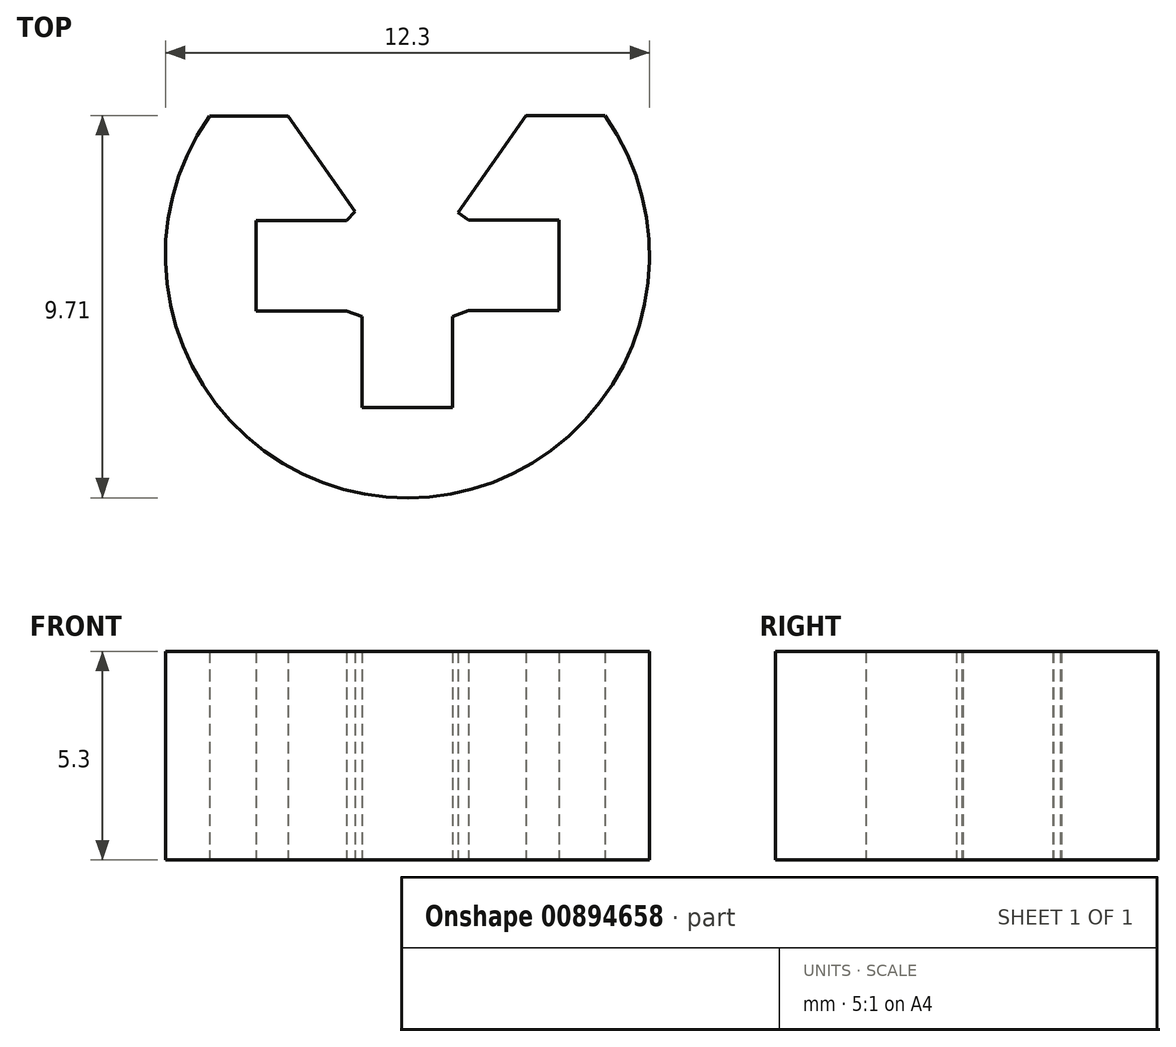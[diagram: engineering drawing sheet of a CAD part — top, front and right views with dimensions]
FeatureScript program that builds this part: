
annotation { "Feature Type Name" : "Feature", "Feature Type Description" : "" }
export const myFeature = defineFeature(function(context is Context, id is Id, definition is map)
    precondition{}
    {
        {
            var Q0;
            Q0=qCreatedBy(makeId("Top.planeOp"),FACE);
            var sketch = newSketch(context, id + "F0", { "sketchPlane" : qUnion([Q0])});
            skCircle(sketch, "E0", {"center": v(0, 0) * mm, "radius": 6.15 * mm});
            skLineSegment(sketch, "E1", {"start": v(-0.01, -0.76) * mm, "end": v(-6.07, 7.88) * mm});
            skLineSegment(sketch, "E2", {"start": v(-6.07, 7.88) * mm, "end": v(6.04, 7.88) * mm});
            skLineSegment(sketch, "E3", {"start": v(6.04, 7.88) * mm, "end": v(-0.01, -0.76) * mm});
            skPoint(sketch, "E4", {"position": v(-0.01, 7.88) * mm});
            skLineSegment(sketch, "E5", {"start": v(-5.03, 3.54) * mm, "end": v(-3.03, 3.54) * mm});
            skLineSegment(sketch, "E6", {"start": v(3.01, 3.56) * mm, "end": v(5.01, 3.56) * mm});
            skArc(sketch, "E7", {"start": v(-3.88, 4.77) * mm, "mid": v(-4.51, 4.21) * mm, "end": v(-5.03, 3.54) * mm});
            skArc(sketch, "E8", {"start": v(5.01, 3.56) * mm, "mid": v(4.46, 4.18) * mm, "end": v(3.87, 4.78) * mm});
            skLineSegment(sketch, "E9.bottom", {"start": v(3.85, 0.91) * mm, "end": v(1.55, 0.91) * mm});
            skLineSegment(sketch, "E9.top", {"start": v(3.85, -1.39) * mm, "end": v(1.55, -1.39) * mm});
            skLineSegment(sketch, "E9.left", {"start": v(3.85, 0.91) * mm, "end": v(3.85, -1.39) * mm});
            skLineSegment(sketch, "E9.right", {"start": v(1.55, 0.91) * mm, "end": v(1.55, -1.39) * mm});
            skPoint(sketch, "E9.middle", {"position": v(2.7, -0.24) * mm});
            skLineSegment(sketch, "E10.bottom", {"start": v(1.15, -3.85) * mm, "end": v(-1.15, -3.85) * mm});
            skLineSegment(sketch, "E10.top", {"start": v(1.15, -1.55) * mm, "end": v(-1.15, -1.55) * mm});
            skLineSegment(sketch, "E10.left", {"start": v(1.15, -3.85) * mm, "end": v(1.15, -1.55) * mm});
            skLineSegment(sketch, "E10.right", {"start": v(-1.15, -3.85) * mm, "end": v(-1.15, -1.55) * mm});
            skPoint(sketch, "E10.middle", {"position": v(0, -2.7) * mm});
            skLineSegment(sketch, "E11.bottom", {"start": v(-1.55, -1.4) * mm, "end": v(-3.85, -1.4) * mm});
            skLineSegment(sketch, "E11.top", {"start": v(-1.55, 0.9) * mm, "end": v(-3.85, 0.9) * mm});
            skLineSegment(sketch, "E11.left", {"start": v(-1.55, -1.4) * mm, "end": v(-1.55, 0.9) * mm});
            skLineSegment(sketch, "E11.right", {"start": v(-3.85, -1.4) * mm, "end": v(-3.85, 0.9) * mm});
            skPoint(sketch, "E11.middle", {"position": v(-2.7, -0.26) * mm});
            skLineSegment(sketch, "E12", {"start": v(-1.55, -1.4) * mm, "end": v(-1.15, -1.55) * mm});
            skLineSegment(sketch, "E13", {"start": v(-1.55, 0.9) * mm, "end": v(-1.27, 1.18) * mm});
            skLineSegment(sketch, "E14", {"start": v(1.55, -1.39) * mm, "end": v(1.15, -1.55) * mm});
            skLineSegment(sketch, "E15", {"start": v(1.55, 0.91) * mm, "end": v(1.16, 1.18) * mm});
            skSolve(sketch);
        }
        {
            var Q0;
            {var subQ2=sQuery(id+"F0.wireOp",EDGE,"E5");Q0=makeQuery(id+"F0.imprint","IMPRINT",FACE,{"disambiguationData":[TD([[makeQuery(id+"F0.imprint","IMPRINT",EDGE,{"derivedFrom":subQ2}),-1.0]])]});}
            extrude(context, id + "F1", {"entities" : qUnion([Q0]), "depth" : 5.3 * mm, "offsetDistance" : 25 * mm});
        }
    });
